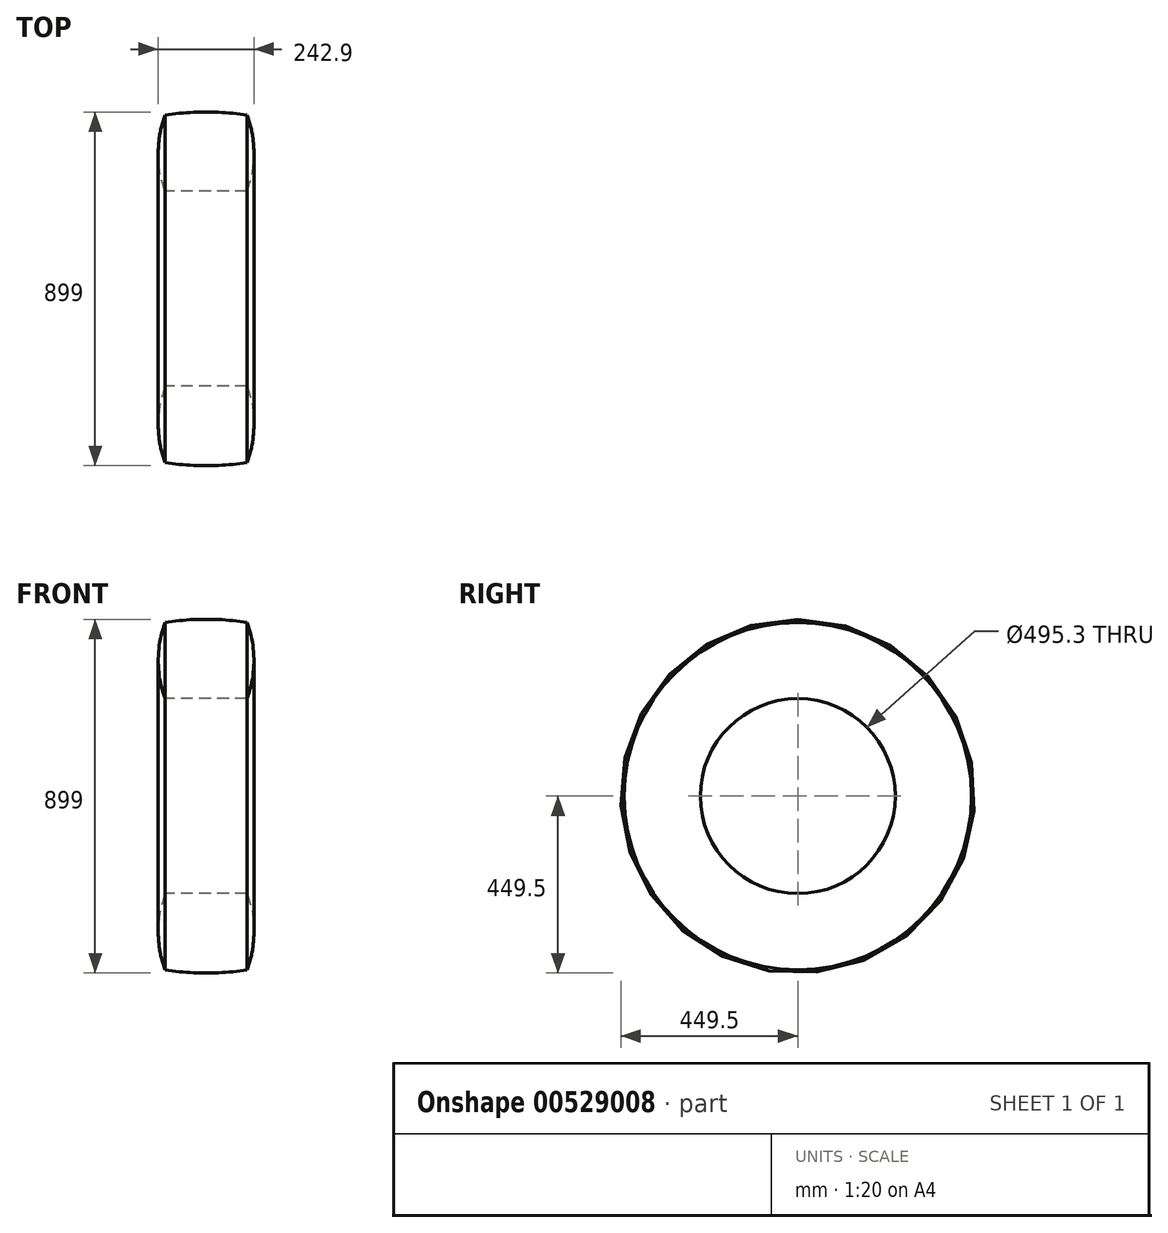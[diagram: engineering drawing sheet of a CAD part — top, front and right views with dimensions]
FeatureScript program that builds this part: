
annotation { "Feature Type Name" : "Feature", "Feature Type Description" : "" }
export const myFeature = defineFeature(function(context is Context, id is Id, definition is map)
    precondition{}
    {
        {
            var Q0;
            Q0=qCreatedBy(makeId("Front.planeOp"),FACE);
            var sketch = newSketch(context, id + "F0", { "sketchPlane" : qUnion([Q0])});
            skLineSegment(sketch, "E0", {"start": v(0, 0) * mm, "end": v(997.5, 0) * mm, "construction": true});
            skLineSegment(sketch, "E1", {"start": v(889.97, 247.65) * mm, "end": v(997.5, 247.65) * mm, "construction": true});
            skLineSegment(sketch, "E2", {"start": v(902.63, 449.5) * mm, "end": v(997.5, 449.5) * mm, "construction": true});
            skLineSegment(sketch, "E3", {"start": v(997.5, 449.5) * mm, "end": v(997.5, 247.65) * mm, "construction": true});
            skArc(sketch, "E4", {"start": v(997.5, 441.5) * mm, "mid": v(893.36, 449.5) * mm, "end": v(789.22, 441.5) * mm});
            skArc(sketch, "E5", {"start": v(997.5, 247.65) * mm, "mid": v(1014.81, 344.57) * mm, "end": v(997.5, 441.5) * mm});
            skLineSegment(sketch, "E6", {"start": v(893.36, 449.5) * mm, "end": v(893.36, 390.8) * mm, "construction": true});
            skArc(sketch, "E7.MirrorCS", {"start": v(789.22, 247.65) * mm, "mid": v(771.9, 344.58) * mm, "end": v(789.22, 441.5) * mm});
            skLineSegment(sketch, "E8", {"start": v(789.22, 247.65) * mm, "end": v(997.5, 247.65) * mm});
            skSolve(sketch);
        }
        {
            var Q0;
            Q0 = qSketchRegion(id + "F0", true);
            var Q1;
            Q1=sQuery(id+"F0.wireOp",EDGE,"E0");
            revolve(context, id + "F1", {"entities" : qUnion([Q0]), "axis" : qUnion([Q1]), "revolveType" : RevolveType.FULL});
        }
    });
